# Revit family: Haworth_Compose_Overhead
name_source: partatom
category: Furniture Systems
revit_build: Autodesk Revit 2018 (Build: 20170223_1515(x64)
units: mm (PartAtom-declared; Revit-internal decimal feet)

## family parameters
Always vertical = Yes
Cut with Voids When Loaded = No
OmniClass Number = 23.40.70.14.64.21
OmniClass Title = Systems Furniture
Part Type = Normal
Room Calculation Point = No
Round Connector Dimension = Use Diameter
Shared = No
Work Plane-Based = No

## types (35) — shared parameters
Assembly Code = E2020200
Back Finish = Haworth _ Laminate _ Linen H-WL
Bracket Finish = Haworth _ Paint _ Metallic Champagne
Custom Size = Yes
Description = Haworth Compose - Overhead
Door Finish = Haworth _ Laminate _ Linen H-WL
Frame Finish = Haworth _ Laminate _ Linen H-WL
Light = No
Light Skirt = No
Manufacturer = Haworth
Max. Depth = 16"
Max. Height = 16 1/2"
Max. Width = 96"
Min. Depth = 6"
Min. Height = 8"
Min. Width = 24"
Min/Max Width = 24-96 in. @ 6 in. increments
Model = Haworth Compose - Overhead
Revision Number = 4
Size = Verify Final Dim. w/ Haworth
Standard Depth = 15 3/4 in.
Standard Heights = 15 3/4 in.
Standard Mount = Yes
Sustainability Info = http://media.haworth.com
URL = www.haworth.com
URL - Product = https://www.haworth.com
Up Mount = No
Warranty = http://www.haworth.com

## per-type parameters (varying)
| type | Actual Depth | Actual Height | Actual Width | Box Depth | Depth | Door Height | Door Width | Flip Door | Height | No Doors | Sliding Door | Width |
| Without Doors 24w 16h | 15 3/4" | 16 1/2" | 24" | 15 3/4" | 15 3/4" | 14 1/2" | 22" | No | 16 1/2" | Yes | No | 24" |
| Without Doors 30w 16h | 15 3/4" | 16 1/2" | 30" | 15 3/4" | 15 3/4" | 14 1/2" | 28" | No | 16 1/2" | Yes | No | 30" |
| Without Doors 36w 16h | 15 3/4" | 16 1/2" | 36" | 15 3/4" | 15 3/4" | 14 1/2" | 34" | No | 16 1/2" | Yes | No | 36" |
| Without Doors 40w 16h | 15 3/4" | 16 1/2" | 40" | 15 3/4" | 15 3/4" | 14 1/2" | 38" | No | 16 1/2" | Yes | No | 40" |
| Without Doors 42w 16h | 15 3/4" | 16 1/2" | 42" | 15 3/4" | 15 3/4" | 14 1/2" | 40" | No | 16 1/2" | Yes | No | 42" |
| Without Doors 48w 16h | 15 3/4" | 16 1/2" | 48" | 15 3/4" | 15 3/4" | 14 1/2" | 46" | No | 16 1/2" | Yes | No | 48" |
| Without Doors 54w 16h | 15 3/4" | 16 1/2" | 54" | 15 3/4" | 15 3/4" | 14 1/2" | 52" | No | 16 1/2" | Yes | No | 54" |
| Without Doors 60w 16h | 15 3/4" | 16 1/2" | 60" | 15 3/4" | 15 3/4" | 14 1/2" | 58" | No | 16 1/2" | Yes | No | 60" |
| Without Doors 66w 16h | 15 3/4" | 16 1/2" | 66" | 15 3/4" | 15 3/4" | 14 1/2" | 64" | No | 16 1/2" | Yes | No | 66" |
| Without Doors 72w 16h | 15 3/4" | 16 1/2" | 72" | 15 3/4" | 15 3/4" | 14 1/2" | 70" | No | 16 1/2" | Yes | No | 72" |
| Without Doors 80w 16h | 15 3/4" | 16 1/2" | 80" | 15 3/4" | 15 3/4" | 14 1/2" | 78" | No | 16 1/2" | Yes | No | 80" |
| Without Doors 84w 16h | 15 3/4" | 16 1/2" | 84" | 15 3/4" | 15 3/4" | 14 1/2" | 82" | No | 16 1/2" | Yes | No | 84" |
| Without Doors 96w 16h | 15 3/4" | 16 1/2" | 96" | 15 3/4" | 15 3/4" | 14 1/2" | 94" | No | 16 1/2" | Yes | No | 96" |
| With Sliding Doors 24w 16h | 15 3/4" | 16 1/2" | 24" | 15 3/4" | 15 3/4" | 14 1/2" | 22" | No | 16 1/2" | No | Yes | 24" |
| With Sliding Doors 30w 16h | 15 3/4" | 16 1/2" | 30" | 15 3/4" | 15 3/4" | 14 1/2" | 28" | No | 16 1/2" | No | Yes | 30" |
| With Sliding Doors 36w 16h | 15 3/4" | 16 1/2" | 36" | 15 3/4" | 15 3/4" | 14 1/2" | 34" | No | 16 1/2" | No | Yes | 36" |
| With Sliding Doors 40w 16h | 15 3/4" | 16 1/2" | 40" | 15 3/4" | 15 3/4" | 14 1/2" | 38" | No | 16 1/2" | No | Yes | 40" |
| With Sliding Doors 42w 16h | 15 3/4" | 16 1/2" | 42" | 15 3/4" | 15 3/4" | 14 1/2" | 40" | No | 16 1/2" | No | Yes | 42" |
| With Sliding Doors 48w 16h | 15 3/4" | 16 1/2" | 48" | 15 3/4" | 15 3/4" | 14 1/2" | 46" | No | 16 1/2" | No | Yes | 48" |
| With Sliding Doors 54w 16h | 15 3/4" | 16 1/2" | 54" | 15 3/4" | 15 3/4" | 14 1/2" | 52" | No | 16 1/2" | No | Yes | 54" |
| With Sliding Doors 60w 16h | 15 3/4" | 16 1/2" | 60" | 15 3/4" | 15 3/4" | 14 1/2" | 58" | No | 16 1/2" | No | Yes | 60" |
| With Sliding Doors 66w 16h | 15 3/4" | 16 1/2" | 66" | 15 3/4" | 15 3/4" | 14 1/2" | 64" | No | 16 1/2" | No | Yes | 66" |
| With Sliding Doors 72w 16h | 15 3/4" | 16 1/2" | 72" | 15 3/4" | 15 3/4" | 14 1/2" | 70" | No | 16 1/2" | No | Yes | 72" |
| With Sliding Doors 80w 16h | 15 3/4" | 16 1/2" | 80" | 15 3/4" | 15 3/4" | 14 1/2" | 78" | No | 16 1/2" | No | Yes | 80" |
| With Sliding Doors 84w 16h | 15 3/4" | 16 1/2" | 84" | 15 3/4" | 15 3/4" | 14 1/2" | 82" | No | 16 1/2" | No | Yes | 84" |
| With Sliding Doors 96w 16h | 15 3/4" | 16 1/2" | 96" | 15 3/4" | 15 3/4" | 14 1/2" | 94" | No | 16 1/2" | No | Yes | 96" |
| With Flip Doors 24w 16h | 14" | 16" | 24" | 14 3/4" | 14" | 14" | 22" | Yes | 16" | No | No | 24" |
| With Flip Doors 30w 16h | 14" | 16" | 30" | 14 3/4" | 14" | 14" | 28" | Yes | 16" | No | No | 30" |
| With Flip Doors 36w 16h | 14" | 16" | 36" | 14 3/4" | 14" | 14" | 34" | Yes | 16" | No | No | 36" |
| With Flip Doors 42w 16h | 14" | 16" | 42" | 14 3/4" | 14" | 14" | 40" | Yes | 16" | No | No | 42" |
| With Flip Doors 48w 16h | 14" | 16" | 48" | 14 3/4" | 14" | 14" | 46" | Yes | 16" | No | No | 48" |
| With Flip Doors 54w 16h | 14" | 16" | 54" | 14 3/4" | 14" | 14" | 52" | Yes | 16" | No | No | 54" |
| With Flip Doors 60w 16h | 14" | 16" | 60" | 14 3/4" | 14" | 14" | 58" | Yes | 16" | No | No | 60" |
| With Flip Doors 66w 16h | 14" | 16" | 66" | 14 3/4" | 14" | 14" | 64" | Yes | 16" | No | No | 66" |
| With Flip Doors 72w 16h | 14" | 16" | 72" | 14 3/4" | 14" | 14" | 70" | Yes | 16" | No | No | 72" |

## geometry (parser evidence)
native form markers: Sweep x13
no freeform markers — native parametric forms only
